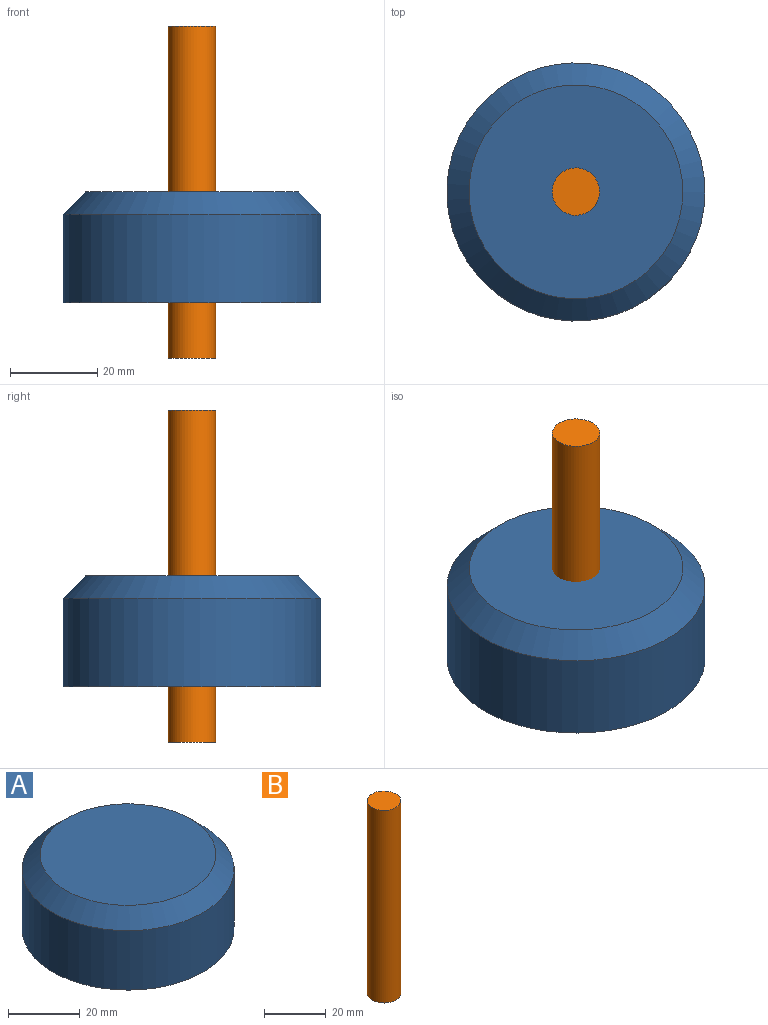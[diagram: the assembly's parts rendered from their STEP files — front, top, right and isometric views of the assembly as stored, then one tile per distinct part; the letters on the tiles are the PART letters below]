
ASSEMBLY  parts=2 mates=1
PART A: 4 faces, bbox 59.2x59.2x25.4 mm
  f0: cylinder r=29.62mm len=59.23mm, axis (0,0,-1), area 3781.2mm2, adj f2,f3
  f1: plane 49.07x49.07mm, normal (0,0,1), area 1891.3mm2, adj f3
  f2: plane 59.23x59.23mm, normal (0,0,-1), area 2755.5mm2, adj f0
  f3: cone r=24.54mm half-angle=45deg, axis (0,0,-1), area 1222.2mm2, adj f0,f1
PART B: 3 faces, bbox 10.9x10.9x76.2 mm
  f0: cylinder r=5.44mm len=76.2mm, axis (0,0,-1), area 2605.4mm2, adj f1,f2
  f1: plane 10.88x10.88mm, normal (0,0,1), area 93mm2, adj f0
  f2: plane 10.88x10.88mm, normal (0,0,-1), area 93mm2, adj f0
PLACE A t=(-81.09,61,-38.38)mm
PLACE B t=(-107.43,112.13,-51.08)mm
MATE slider B.f0 <-> A.f0  axis (0,0,-1) through (9.21,71.48,-12.98)mm
